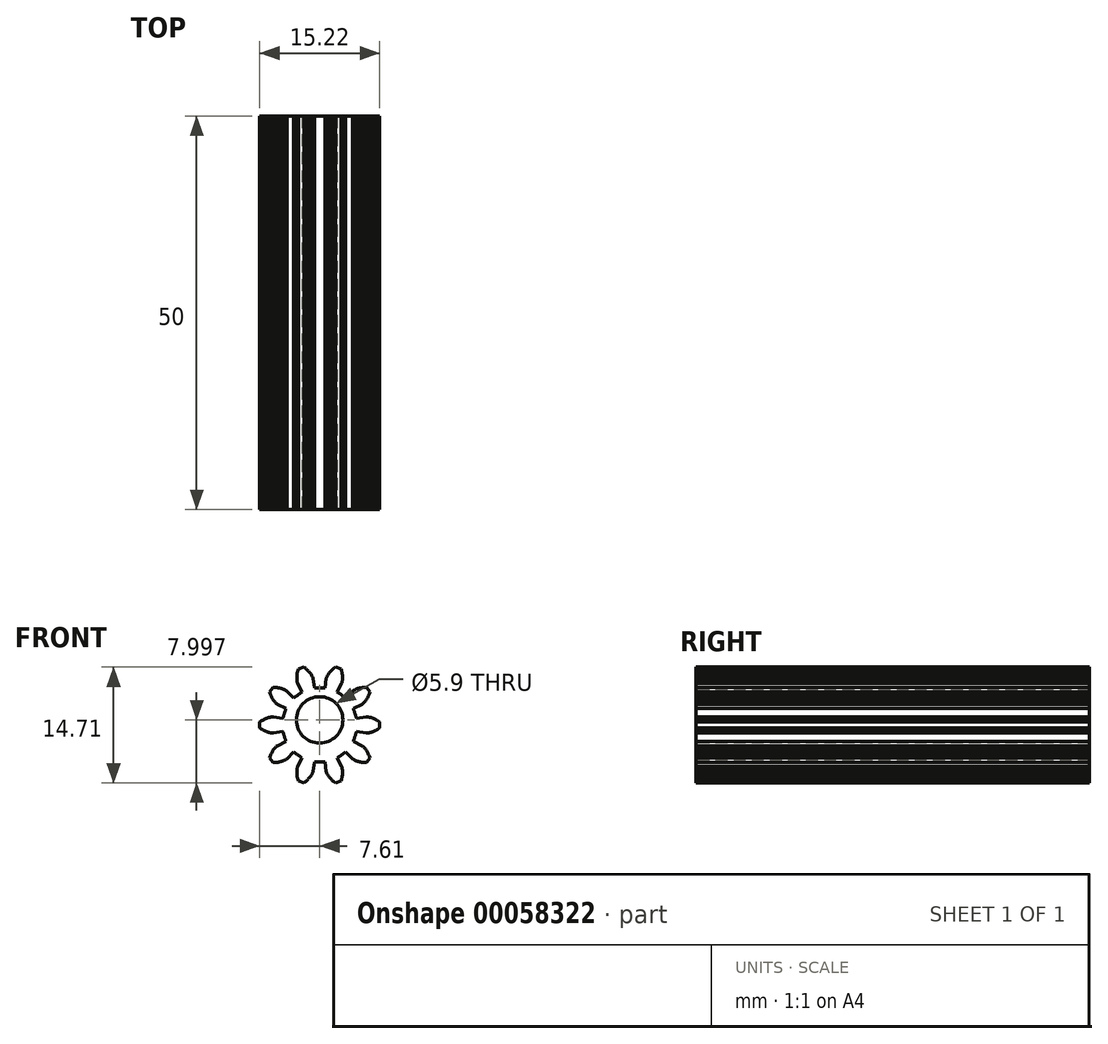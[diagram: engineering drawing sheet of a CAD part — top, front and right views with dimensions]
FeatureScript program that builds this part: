
annotation { "Feature Type Name" : "Feature", "Feature Type Description" : "" }
export const myFeature = defineFeature(function(context is Context, id is Id, definition is map)
    precondition{}
    {
        {
            var Q0;
            Q0=qCreatedBy(makeId("Front.planeOp"),FACE);
            var sketch = newSketch(context, id + "F0", { "sketchPlane" : qUnion([Q0])});
            skLineSegment(sketch, "E0", {"start": v(4.7, 0.36) * mm, "end": v(5.88, 0.15) * mm});
            skLineSegment(sketch, "E1", {"start": v(5.88, 0.15) * mm, "end": v(5.98, 0.15) * mm});
            skLineSegment(sketch, "E2", {"start": v(5.98, 0.15) * mm, "end": v(6.08, 0.15) * mm});
            skLineSegment(sketch, "E3", {"start": v(6.08, 0.15) * mm, "end": v(6.19, 0.17) * mm});
            skLineSegment(sketch, "E4", {"start": v(6.19, 0.17) * mm, "end": v(6.3, 0.19) * mm});
            skLineSegment(sketch, "E5", {"start": v(6.3, 0.19) * mm, "end": v(6.4, 0.2) * mm});
            skLineSegment(sketch, "E6", {"start": v(6.4, 0.2) * mm, "end": v(6.5, 0.24) * mm});
            skLineSegment(sketch, "E7", {"start": v(6.5, 0.24) * mm, "end": v(6.63, 0.28) * mm});
            skLineSegment(sketch, "E8", {"start": v(6.63, 0.28) * mm, "end": v(6.73, 0.32) * mm});
            skLineSegment(sketch, "E9", {"start": v(6.73, 0.32) * mm, "end": v(6.84, 0.36) * mm});
            skLineSegment(sketch, "E10", {"start": v(6.84, 0.36) * mm, "end": v(6.95, 0.4) * mm});
            skLineSegment(sketch, "E11", {"start": v(6.95, 0.4) * mm, "end": v(7.07, 0.47) * mm});
            skLineSegment(sketch, "E12", {"start": v(7.07, 0.47) * mm, "end": v(7.16, 0.52) * mm});
            skLineSegment(sketch, "E13", {"start": v(7.16, 0.52) * mm, "end": v(7.25, 0.57) * mm});
            skLineSegment(sketch, "E14", {"start": v(7.25, 0.57) * mm, "end": v(7.35, 0.63) * mm});
            skLineSegment(sketch, "E15", {"start": v(7.35, 0.63) * mm, "end": v(7.44, 0.69) * mm});
            skLineSegment(sketch, "E16", {"start": v(7.44, 0.69) * mm, "end": v(7.61, 0.8) * mm});
            skLineSegment(sketch, "E17", {"start": v(7.61, 0.8) * mm, "end": v(7.61, 1.55) * mm});
            skLineSegment(sketch, "E18", {"start": v(7.61, 1.55) * mm, "end": v(7.44, 1.66) * mm});
            skLineSegment(sketch, "E19", {"start": v(7.44, 1.66) * mm, "end": v(7.35, 1.72) * mm});
            skLineSegment(sketch, "E20", {"start": v(7.35, 1.72) * mm, "end": v(7.25, 1.78) * mm});
            skLineSegment(sketch, "E21", {"start": v(7.25, 1.78) * mm, "end": v(7.16, 1.83) * mm});
            skLineSegment(sketch, "E22", {"start": v(7.16, 1.83) * mm, "end": v(7.07, 1.88) * mm});
            skLineSegment(sketch, "E23", {"start": v(7.07, 1.88) * mm, "end": v(6.95, 1.94) * mm});
            skLineSegment(sketch, "E24", {"start": v(6.95, 1.94) * mm, "end": v(6.84, 1.99) * mm});
            skLineSegment(sketch, "E25", {"start": v(6.84, 1.99) * mm, "end": v(6.73, 2.03) * mm});
            skLineSegment(sketch, "E26", {"start": v(6.73, 2.03) * mm, "end": v(6.63, 2.07) * mm});
            skLineSegment(sketch, "E27", {"start": v(6.63, 2.07) * mm, "end": v(6.5, 2.1) * mm});
            skLineSegment(sketch, "E28", {"start": v(6.5, 2.1) * mm, "end": v(6.4, 2.14) * mm});
            skLineSegment(sketch, "E29", {"start": v(6.4, 2.14) * mm, "end": v(6.3, 2.16) * mm});
            skLineSegment(sketch, "E30", {"start": v(6.3, 2.16) * mm, "end": v(6.19, 2.18) * mm});
            skLineSegment(sketch, "E31", {"start": v(6.19, 2.18) * mm, "end": v(6.08, 2.2) * mm});
            skLineSegment(sketch, "E32", {"start": v(6.08, 2.2) * mm, "end": v(5.98, 2.2) * mm});
            skLineSegment(sketch, "E33", {"start": v(5.98, 2.2) * mm, "end": v(5.88, 2.2) * mm});
            skLineSegment(sketch, "E34", {"start": v(5.88, 2.2) * mm, "end": v(4.7, 1.99) * mm});
            skArc(sketch, "E35", {"start": v(4.7, 1.99) * mm, "mid": v(4.48, 2.63) * mm, "end": v(4.28, 3.27) * mm});
            skLineSegment(sketch, "E36", {"start": v(4.28, 3.27) * mm, "end": v(5.36, 3.8) * mm});
            skLineSegment(sketch, "E37", {"start": v(5.36, 3.8) * mm, "end": v(5.44, 3.86) * mm});
            skLineSegment(sketch, "E38", {"start": v(5.44, 3.86) * mm, "end": v(5.52, 3.92) * mm});
            skLineSegment(sketch, "E39", {"start": v(5.52, 3.92) * mm, "end": v(5.6, 4) * mm});
            skLineSegment(sketch, "E40", {"start": v(5.6, 4) * mm, "end": v(5.67, 4.08) * mm});
            skLineSegment(sketch, "E41", {"start": v(5.67, 4.08) * mm, "end": v(5.74, 4.15) * mm});
            skLineSegment(sketch, "E42", {"start": v(5.74, 4.15) * mm, "end": v(5.81, 4.24) * mm});
            skLineSegment(sketch, "E43", {"start": v(5.81, 4.24) * mm, "end": v(5.89, 4.34) * mm});
            skLineSegment(sketch, "E44", {"start": v(5.89, 4.34) * mm, "end": v(5.95, 4.44) * mm});
            skLineSegment(sketch, "E45", {"start": v(5.95, 4.44) * mm, "end": v(6.01, 4.53) * mm});
            skLineSegment(sketch, "E46", {"start": v(6.01, 4.53) * mm, "end": v(6.07, 4.64) * mm});
            skLineSegment(sketch, "E47", {"start": v(6.07, 4.64) * mm, "end": v(6.13, 4.76) * mm});
            skLineSegment(sketch, "E48", {"start": v(6.13, 4.76) * mm, "end": v(6.18, 4.85) * mm});
            skLineSegment(sketch, "E49", {"start": v(6.18, 4.85) * mm, "end": v(6.22, 4.95) * mm});
            skLineSegment(sketch, "E50", {"start": v(6.22, 4.95) * mm, "end": v(6.27, 5.05) * mm});
            skLineSegment(sketch, "E51", {"start": v(6.27, 5.05) * mm, "end": v(6.3, 5.16) * mm});
            skLineSegment(sketch, "E52", {"start": v(6.3, 5.16) * mm, "end": v(6.38, 5.35) * mm});
            skLineSegment(sketch, "E53", {"start": v(6.38, 5.35) * mm, "end": v(5.94, 5.95) * mm});
            skLineSegment(sketch, "E54", {"start": v(5.94, 5.95) * mm, "end": v(5.74, 5.94) * mm});
            skLineSegment(sketch, "E55", {"start": v(5.74, 5.94) * mm, "end": v(5.62, 5.94) * mm});
            skLineSegment(sketch, "E56", {"start": v(5.62, 5.94) * mm, "end": v(5.51, 5.93) * mm});
            skLineSegment(sketch, "E57", {"start": v(5.51, 5.93) * mm, "end": v(5.4, 5.92) * mm});
            skLineSegment(sketch, "E58", {"start": v(5.4, 5.92) * mm, "end": v(5.3, 5.9) * mm});
            skLineSegment(sketch, "E59", {"start": v(5.3, 5.9) * mm, "end": v(5.17, 5.88) * mm});
            skLineSegment(sketch, "E60", {"start": v(5.17, 5.88) * mm, "end": v(5.05, 5.85) * mm});
            skLineSegment(sketch, "E61", {"start": v(5.05, 5.85) * mm, "end": v(4.94, 5.83) * mm});
            skLineSegment(sketch, "E62", {"start": v(4.94, 5.83) * mm, "end": v(4.83, 5.8) * mm});
            skLineSegment(sketch, "E63", {"start": v(4.83, 5.8) * mm, "end": v(4.71, 5.76) * mm});
            skLineSegment(sketch, "E64", {"start": v(4.71, 5.76) * mm, "end": v(4.6, 5.72) * mm});
            skLineSegment(sketch, "E65", {"start": v(4.6, 5.72) * mm, "end": v(4.51, 5.68) * mm});
            skLineSegment(sketch, "E66", {"start": v(4.51, 5.68) * mm, "end": v(4.41, 5.63) * mm});
            skLineSegment(sketch, "E67", {"start": v(4.41, 5.63) * mm, "end": v(4.32, 5.58) * mm});
            skLineSegment(sketch, "E68", {"start": v(4.32, 5.58) * mm, "end": v(4.23, 5.52) * mm});
            skLineSegment(sketch, "E69", {"start": v(4.23, 5.52) * mm, "end": v(4.16, 5.46) * mm});
            skLineSegment(sketch, "E70", {"start": v(4.16, 5.46) * mm, "end": v(3.32, 4.6) * mm});
            skArc(sketch, "E71", {"start": v(3.32, 4.6) * mm, "mid": v(2.77, 4.99) * mm, "end": v(2.23, 5.39) * mm});
            skLineSegment(sketch, "E72", {"start": v(2.23, 5.39) * mm, "end": v(2.79, 6.45) * mm});
            skLineSegment(sketch, "E73", {"start": v(2.79, 6.45) * mm, "end": v(2.82, 6.54) * mm});
            skLineSegment(sketch, "E74", {"start": v(2.82, 6.54) * mm, "end": v(2.85, 6.64) * mm});
            skLineSegment(sketch, "E75", {"start": v(2.85, 6.64) * mm, "end": v(2.87, 6.75) * mm});
            skLineSegment(sketch, "E76", {"start": v(2.87, 6.75) * mm, "end": v(2.89, 6.86) * mm});
            skLineSegment(sketch, "E77", {"start": v(2.89, 6.86) * mm, "end": v(2.9, 6.96) * mm});
            skLineSegment(sketch, "E78", {"start": v(2.9, 6.96) * mm, "end": v(2.9, 7.07) * mm});
            skLineSegment(sketch, "E79", {"start": v(2.9, 7.07) * mm, "end": v(2.9, 7.2) * mm});
            skLineSegment(sketch, "E80", {"start": v(2.9, 7.2) * mm, "end": v(2.9, 7.3) * mm});
            skLineSegment(sketch, "E81", {"start": v(2.9, 7.3) * mm, "end": v(2.89, 7.43) * mm});
            skLineSegment(sketch, "E82", {"start": v(2.89, 7.43) * mm, "end": v(2.87, 7.55) * mm});
            skLineSegment(sketch, "E83", {"start": v(2.87, 7.55) * mm, "end": v(2.86, 7.68) * mm});
            skLineSegment(sketch, "E84", {"start": v(2.86, 7.68) * mm, "end": v(2.84, 7.78) * mm});
            skLineSegment(sketch, "E85", {"start": v(2.84, 7.78) * mm, "end": v(2.82, 7.88) * mm});
            skLineSegment(sketch, "E86", {"start": v(2.82, 7.88) * mm, "end": v(2.8, 8) * mm});
            skLineSegment(sketch, "E87", {"start": v(2.8, 8) * mm, "end": v(2.76, 8.1) * mm});
            skLineSegment(sketch, "E88", {"start": v(2.76, 8.1) * mm, "end": v(2.7, 8.3) * mm});
            skLineSegment(sketch, "E89", {"start": v(2.7, 8.3) * mm, "end": v(2, 8.53) * mm});
            skLineSegment(sketch, "E90", {"start": v(2, 8.53) * mm, "end": v(1.84, 8.4) * mm});
            skLineSegment(sketch, "E91", {"start": v(1.84, 8.4) * mm, "end": v(1.75, 8.33) * mm});
            skLineSegment(sketch, "E92", {"start": v(1.75, 8.33) * mm, "end": v(1.66, 8.26) * mm});
            skLineSegment(sketch, "E93", {"start": v(1.66, 8.26) * mm, "end": v(1.59, 8.19) * mm});
            skLineSegment(sketch, "E94", {"start": v(1.59, 8.19) * mm, "end": v(1.51, 8.11) * mm});
            skLineSegment(sketch, "E95", {"start": v(1.51, 8.11) * mm, "end": v(1.42, 8.02) * mm});
            skLineSegment(sketch, "E96", {"start": v(1.42, 8.02) * mm, "end": v(1.34, 7.93) * mm});
            skLineSegment(sketch, "E97", {"start": v(1.34, 7.93) * mm, "end": v(1.26, 7.84) * mm});
            skLineSegment(sketch, "E98", {"start": v(1.26, 7.84) * mm, "end": v(1.2, 7.75) * mm});
            skLineSegment(sketch, "E99", {"start": v(1.2, 7.75) * mm, "end": v(1.12, 7.65) * mm});
            skLineSegment(sketch, "E100", {"start": v(1.12, 7.65) * mm, "end": v(1.06, 7.56) * mm});
            skLineSegment(sketch, "E101", {"start": v(1.06, 7.56) * mm, "end": v(1, 7.47) * mm});
            skLineSegment(sketch, "E102", {"start": v(1, 7.47) * mm, "end": v(0.95, 7.37) * mm});
            skLineSegment(sketch, "E103", {"start": v(0.95, 7.37) * mm, "end": v(0.9, 7.28) * mm});
            skLineSegment(sketch, "E104", {"start": v(0.9, 7.28) * mm, "end": v(0.87, 7.18) * mm});
            skLineSegment(sketch, "E105", {"start": v(0.87, 7.18) * mm, "end": v(0.85, 7.08) * mm});
            skLineSegment(sketch, "E106", {"start": v(0.85, 7.08) * mm, "end": v(0.67, 5.89) * mm});
            skArc(sketch, "E107", {"start": v(0.67, 5.89) * mm, "mid": v(0, 5.89) * mm, "end": v(-0.67, 5.89) * mm});
            skLineSegment(sketch, "E108", {"start": v(-0.67, 5.89) * mm, "end": v(-0.85, 7.08) * mm});
            skLineSegment(sketch, "E109", {"start": v(-0.85, 7.08) * mm, "end": v(-0.87, 7.18) * mm});
            skLineSegment(sketch, "E110", {"start": v(-0.87, 7.18) * mm, "end": v(-0.9, 7.28) * mm});
            skLineSegment(sketch, "E111", {"start": v(-0.9, 7.28) * mm, "end": v(-0.95, 7.37) * mm});
            skLineSegment(sketch, "E112", {"start": v(-0.95, 7.37) * mm, "end": v(-1, 7.47) * mm});
            skLineSegment(sketch, "E113", {"start": v(-1, 7.47) * mm, "end": v(-1.06, 7.56) * mm});
            skLineSegment(sketch, "E114", {"start": v(-1.06, 7.56) * mm, "end": v(-1.12, 7.65) * mm});
            skLineSegment(sketch, "E115", {"start": v(-1.12, 7.65) * mm, "end": v(-1.2, 7.75) * mm});
            skLineSegment(sketch, "E116", {"start": v(-1.2, 7.75) * mm, "end": v(-1.26, 7.84) * mm});
            skLineSegment(sketch, "E117", {"start": v(-1.26, 7.84) * mm, "end": v(-1.34, 7.93) * mm});
            skLineSegment(sketch, "E118", {"start": v(-1.34, 7.93) * mm, "end": v(-1.42, 8.02) * mm});
            skLineSegment(sketch, "E119", {"start": v(-1.42, 8.02) * mm, "end": v(-1.51, 8.11) * mm});
            skLineSegment(sketch, "E120", {"start": v(-1.51, 8.11) * mm, "end": v(-1.59, 8.19) * mm});
            skLineSegment(sketch, "E121", {"start": v(-1.59, 8.19) * mm, "end": v(-1.66, 8.26) * mm});
            skLineSegment(sketch, "E122", {"start": v(-1.66, 8.26) * mm, "end": v(-1.75, 8.33) * mm});
            skLineSegment(sketch, "E123", {"start": v(-1.75, 8.33) * mm, "end": v(-1.84, 8.4) * mm});
            skLineSegment(sketch, "E124", {"start": v(-1.84, 8.4) * mm, "end": v(-2, 8.53) * mm});
            skLineSegment(sketch, "E125", {"start": v(-2, 8.53) * mm, "end": v(-2.7, 8.3) * mm});
            skLineSegment(sketch, "E126", {"start": v(-2.7, 8.3) * mm, "end": v(-2.76, 8.1) * mm});
            skLineSegment(sketch, "E127", {"start": v(-2.76, 8.1) * mm, "end": v(-2.8, 8) * mm});
            skLineSegment(sketch, "E128", {"start": v(-2.8, 8) * mm, "end": v(-2.82, 7.88) * mm});
            skLineSegment(sketch, "E129", {"start": v(-2.82, 7.88) * mm, "end": v(-2.84, 7.78) * mm});
            skLineSegment(sketch, "E130", {"start": v(-2.84, 7.78) * mm, "end": v(-2.86, 7.68) * mm});
            skLineSegment(sketch, "E131", {"start": v(-2.86, 7.68) * mm, "end": v(-2.87, 7.55) * mm});
            skLineSegment(sketch, "E132", {"start": v(-2.87, 7.55) * mm, "end": v(-2.89, 7.43) * mm});
            skLineSegment(sketch, "E133", {"start": v(-2.89, 7.43) * mm, "end": v(-2.9, 7.3) * mm});
            skLineSegment(sketch, "E134", {"start": v(-2.9, 7.3) * mm, "end": v(-2.9, 7.2) * mm});
            skLineSegment(sketch, "E135", {"start": v(-2.9, 7.2) * mm, "end": v(-2.9, 7.07) * mm});
            skLineSegment(sketch, "E136", {"start": v(-2.9, 7.07) * mm, "end": v(-2.9, 6.96) * mm});
            skLineSegment(sketch, "E137", {"start": v(-2.9, 6.96) * mm, "end": v(-2.89, 6.86) * mm});
            skLineSegment(sketch, "E138", {"start": v(-2.89, 6.86) * mm, "end": v(-2.87, 6.75) * mm});
            skLineSegment(sketch, "E139", {"start": v(-2.87, 6.75) * mm, "end": v(-2.85, 6.64) * mm});
            skLineSegment(sketch, "E140", {"start": v(-2.85, 6.64) * mm, "end": v(-2.82, 6.54) * mm});
            skLineSegment(sketch, "E141", {"start": v(-2.82, 6.54) * mm, "end": v(-2.79, 6.45) * mm});
            skLineSegment(sketch, "E142", {"start": v(-2.79, 6.45) * mm, "end": v(-2.23, 5.39) * mm});
            skArc(sketch, "E143", {"start": v(-2.23, 5.39) * mm, "mid": v(-2.77, 4.99) * mm, "end": v(-3.32, 4.6) * mm});
            skLineSegment(sketch, "E144", {"start": v(-3.32, 4.6) * mm, "end": v(-4.16, 5.46) * mm});
            skLineSegment(sketch, "E145", {"start": v(-4.16, 5.46) * mm, "end": v(-4.23, 5.52) * mm});
            skLineSegment(sketch, "E146", {"start": v(-4.23, 5.52) * mm, "end": v(-4.32, 5.58) * mm});
            skLineSegment(sketch, "E147", {"start": v(-4.32, 5.58) * mm, "end": v(-4.41, 5.63) * mm});
            skLineSegment(sketch, "E148", {"start": v(-4.41, 5.63) * mm, "end": v(-4.51, 5.68) * mm});
            skLineSegment(sketch, "E149", {"start": v(-4.51, 5.68) * mm, "end": v(-4.6, 5.72) * mm});
            skLineSegment(sketch, "E150", {"start": v(-4.6, 5.72) * mm, "end": v(-4.71, 5.76) * mm});
            skLineSegment(sketch, "E151", {"start": v(-4.71, 5.76) * mm, "end": v(-4.83, 5.8) * mm});
            skLineSegment(sketch, "E152", {"start": v(-4.83, 5.8) * mm, "end": v(-4.94, 5.83) * mm});
            skLineSegment(sketch, "E153", {"start": v(-4.94, 5.83) * mm, "end": v(-5.05, 5.85) * mm});
            skLineSegment(sketch, "E154", {"start": v(-5.05, 5.85) * mm, "end": v(-5.17, 5.88) * mm});
            skLineSegment(sketch, "E155", {"start": v(-5.17, 5.88) * mm, "end": v(-5.3, 5.9) * mm});
            skLineSegment(sketch, "E156", {"start": v(-5.3, 5.9) * mm, "end": v(-5.4, 5.92) * mm});
            skLineSegment(sketch, "E157", {"start": v(-5.4, 5.92) * mm, "end": v(-5.51, 5.93) * mm});
            skLineSegment(sketch, "E158", {"start": v(-5.51, 5.93) * mm, "end": v(-5.62, 5.94) * mm});
            skLineSegment(sketch, "E159", {"start": v(-5.62, 5.94) * mm, "end": v(-5.74, 5.94) * mm});
            skLineSegment(sketch, "E160", {"start": v(-5.74, 5.94) * mm, "end": v(-5.94, 5.95) * mm});
            skLineSegment(sketch, "E161", {"start": v(-5.94, 5.95) * mm, "end": v(-6.38, 5.35) * mm});
            skLineSegment(sketch, "E162", {"start": v(-6.38, 5.35) * mm, "end": v(-6.3, 5.16) * mm});
            skLineSegment(sketch, "E163", {"start": v(-6.3, 5.16) * mm, "end": v(-6.27, 5.05) * mm});
            skLineSegment(sketch, "E164", {"start": v(-6.27, 5.05) * mm, "end": v(-6.22, 4.95) * mm});
            skLineSegment(sketch, "E165", {"start": v(-6.22, 4.95) * mm, "end": v(-6.18, 4.85) * mm});
            skLineSegment(sketch, "E166", {"start": v(-6.18, 4.85) * mm, "end": v(-6.13, 4.76) * mm});
            skLineSegment(sketch, "E167", {"start": v(-6.13, 4.76) * mm, "end": v(-6.07, 4.64) * mm});
            skLineSegment(sketch, "E168", {"start": v(-6.07, 4.64) * mm, "end": v(-6.01, 4.53) * mm});
            skLineSegment(sketch, "E169", {"start": v(-6.01, 4.53) * mm, "end": v(-5.95, 4.44) * mm});
            skLineSegment(sketch, "E170", {"start": v(-5.95, 4.44) * mm, "end": v(-5.89, 4.34) * mm});
            skLineSegment(sketch, "E171", {"start": v(-5.89, 4.34) * mm, "end": v(-5.81, 4.24) * mm});
            skLineSegment(sketch, "E172", {"start": v(-5.81, 4.24) * mm, "end": v(-5.74, 4.15) * mm});
            skLineSegment(sketch, "E173", {"start": v(-5.74, 4.15) * mm, "end": v(-5.67, 4.08) * mm});
            skLineSegment(sketch, "E174", {"start": v(-5.67, 4.08) * mm, "end": v(-5.6, 4) * mm});
            skLineSegment(sketch, "E175", {"start": v(-5.6, 4) * mm, "end": v(-5.52, 3.92) * mm});
            skLineSegment(sketch, "E176", {"start": v(-5.52, 3.92) * mm, "end": v(-5.44, 3.86) * mm});
            skLineSegment(sketch, "E177", {"start": v(-5.44, 3.86) * mm, "end": v(-5.36, 3.8) * mm});
            skLineSegment(sketch, "E178", {"start": v(-5.36, 3.8) * mm, "end": v(-4.28, 3.27) * mm});
            skArc(sketch, "E179", {"start": v(-4.28, 3.27) * mm, "mid": v(-4.48, 2.63) * mm, "end": v(-4.7, 1.99) * mm});
            skLineSegment(sketch, "E180", {"start": v(-4.7, 1.99) * mm, "end": v(-5.88, 2.2) * mm});
            skLineSegment(sketch, "E181", {"start": v(-5.88, 2.2) * mm, "end": v(-5.98, 2.2) * mm});
            skLineSegment(sketch, "E182", {"start": v(-5.98, 2.2) * mm, "end": v(-6.08, 2.2) * mm});
            skLineSegment(sketch, "E183", {"start": v(-6.08, 2.2) * mm, "end": v(-6.19, 2.18) * mm});
            skLineSegment(sketch, "E184", {"start": v(-6.19, 2.18) * mm, "end": v(-6.3, 2.16) * mm});
            skLineSegment(sketch, "E185", {"start": v(-6.3, 2.16) * mm, "end": v(-6.4, 2.14) * mm});
            skLineSegment(sketch, "E186", {"start": v(-6.4, 2.14) * mm, "end": v(-6.5, 2.1) * mm});
            skLineSegment(sketch, "E187", {"start": v(-6.5, 2.1) * mm, "end": v(-6.63, 2.07) * mm});
            skLineSegment(sketch, "E188", {"start": v(-6.63, 2.07) * mm, "end": v(-6.73, 2.03) * mm});
            skLineSegment(sketch, "E189", {"start": v(-6.73, 2.03) * mm, "end": v(-6.84, 1.99) * mm});
            skLineSegment(sketch, "E190", {"start": v(-6.84, 1.99) * mm, "end": v(-6.95, 1.94) * mm});
            skLineSegment(sketch, "E191", {"start": v(-6.95, 1.94) * mm, "end": v(-7.07, 1.88) * mm});
            skLineSegment(sketch, "E192", {"start": v(-7.07, 1.88) * mm, "end": v(-7.16, 1.83) * mm});
            skLineSegment(sketch, "E193", {"start": v(-7.16, 1.83) * mm, "end": v(-7.25, 1.78) * mm});
            skLineSegment(sketch, "E194", {"start": v(-7.25, 1.78) * mm, "end": v(-7.35, 1.72) * mm});
            skLineSegment(sketch, "E195", {"start": v(-7.35, 1.72) * mm, "end": v(-7.44, 1.66) * mm});
            skLineSegment(sketch, "E196", {"start": v(-7.44, 1.66) * mm, "end": v(-7.61, 1.55) * mm});
            skLineSegment(sketch, "E197", {"start": v(-7.61, 1.55) * mm, "end": v(-7.61, 0.8) * mm});
            skLineSegment(sketch, "E198", {"start": v(-7.61, 0.8) * mm, "end": v(-7.44, 0.69) * mm});
            skLineSegment(sketch, "E199", {"start": v(-7.44, 0.69) * mm, "end": v(-7.35, 0.63) * mm});
            skLineSegment(sketch, "E200", {"start": v(-7.35, 0.63) * mm, "end": v(-7.25, 0.57) * mm});
            skLineSegment(sketch, "E201", {"start": v(-7.25, 0.57) * mm, "end": v(-7.16, 0.52) * mm});
            skLineSegment(sketch, "E202", {"start": v(-7.16, 0.52) * mm, "end": v(-7.07, 0.47) * mm});
            skLineSegment(sketch, "E203", {"start": v(-7.07, 0.47) * mm, "end": v(-6.95, 0.4) * mm});
            skLineSegment(sketch, "E204", {"start": v(-6.95, 0.4) * mm, "end": v(-6.84, 0.36) * mm});
            skLineSegment(sketch, "E205", {"start": v(-6.84, 0.36) * mm, "end": v(-6.73, 0.32) * mm});
            skLineSegment(sketch, "E206", {"start": v(-6.73, 0.32) * mm, "end": v(-6.63, 0.28) * mm});
            skLineSegment(sketch, "E207", {"start": v(-6.63, 0.28) * mm, "end": v(-6.5, 0.24) * mm});
            skLineSegment(sketch, "E208", {"start": v(-6.5, 0.24) * mm, "end": v(-6.4, 0.2) * mm});
            skLineSegment(sketch, "E209", {"start": v(-6.4, 0.2) * mm, "end": v(-6.3, 0.19) * mm});
            skLineSegment(sketch, "E210", {"start": v(-6.3, 0.19) * mm, "end": v(-6.19, 0.17) * mm});
            skLineSegment(sketch, "E211", {"start": v(-6.19, 0.17) * mm, "end": v(-6.08, 0.15) * mm});
            skLineSegment(sketch, "E212", {"start": v(-6.08, 0.15) * mm, "end": v(-5.98, 0.15) * mm});
            skLineSegment(sketch, "E213", {"start": v(-5.98, 0.15) * mm, "end": v(-5.88, 0.15) * mm});
            skLineSegment(sketch, "E214", {"start": v(-5.88, 0.15) * mm, "end": v(-4.7, 0.36) * mm});
            skArc(sketch, "E215", {"start": v(-4.7, 0.36) * mm, "mid": v(-4.48, -0.28) * mm, "end": v(-4.28, -0.92) * mm});
            skLineSegment(sketch, "E216", {"start": v(-4.28, -0.92) * mm, "end": v(-5.36, -1.45) * mm});
            skLineSegment(sketch, "E217", {"start": v(-5.36, -1.45) * mm, "end": v(-5.44, -1.5) * mm});
            skLineSegment(sketch, "E218", {"start": v(-5.44, -1.5) * mm, "end": v(-5.52, -1.57) * mm});
            skLineSegment(sketch, "E219", {"start": v(-5.52, -1.57) * mm, "end": v(-5.6, -1.65) * mm});
            skLineSegment(sketch, "E220", {"start": v(-5.6, -1.65) * mm, "end": v(-5.67, -1.73) * mm});
            skLineSegment(sketch, "E221", {"start": v(-5.67, -1.73) * mm, "end": v(-5.74, -1.8) * mm});
            skLineSegment(sketch, "E222", {"start": v(-5.74, -1.8) * mm, "end": v(-5.81, -1.9) * mm});
            skLineSegment(sketch, "E223", {"start": v(-5.81, -1.9) * mm, "end": v(-5.89, -2) * mm});
            skLineSegment(sketch, "E224", {"start": v(-5.89, -2) * mm, "end": v(-5.95, -2.09) * mm});
            skLineSegment(sketch, "E225", {"start": v(-5.95, -2.09) * mm, "end": v(-6.01, -2.18) * mm});
            skLineSegment(sketch, "E226", {"start": v(-6.01, -2.18) * mm, "end": v(-6.07, -2.3) * mm});
            skLineSegment(sketch, "E227", {"start": v(-6.07, -2.3) * mm, "end": v(-6.13, -2.4) * mm});
            skLineSegment(sketch, "E228", {"start": v(-6.13, -2.4) * mm, "end": v(-6.18, -2.5) * mm});
            skLineSegment(sketch, "E229", {"start": v(-6.18, -2.5) * mm, "end": v(-6.22, -2.6) * mm});
            skLineSegment(sketch, "E230", {"start": v(-6.22, -2.6) * mm, "end": v(-6.27, -2.7) * mm});
            skLineSegment(sketch, "E231", {"start": v(-6.27, -2.7) * mm, "end": v(-6.3, -2.8) * mm});
            skLineSegment(sketch, "E232", {"start": v(-6.3, -2.8) * mm, "end": v(-6.38, -3) * mm});
            skLineSegment(sketch, "E233", {"start": v(-6.38, -3) * mm, "end": v(-5.94, -3.6) * mm});
            skLineSegment(sketch, "E234", {"start": v(-5.94, -3.6) * mm, "end": v(-5.74, -3.6) * mm});
            skLineSegment(sketch, "E235", {"start": v(-5.74, -3.6) * mm, "end": v(-5.62, -3.59) * mm});
            skLineSegment(sketch, "E236", {"start": v(-5.62, -3.59) * mm, "end": v(-5.51, -3.58) * mm});
            skLineSegment(sketch, "E237", {"start": v(-5.51, -3.58) * mm, "end": v(-5.4, -3.57) * mm});
            skLineSegment(sketch, "E238", {"start": v(-5.4, -3.57) * mm, "end": v(-5.3, -3.55) * mm});
            skLineSegment(sketch, "E239", {"start": v(-5.3, -3.55) * mm, "end": v(-5.17, -3.53) * mm});
            skLineSegment(sketch, "E240", {"start": v(-5.17, -3.53) * mm, "end": v(-5.05, -3.5) * mm});
            skLineSegment(sketch, "E241", {"start": v(-5.05, -3.5) * mm, "end": v(-4.94, -3.48) * mm});
            skLineSegment(sketch, "E242", {"start": v(-4.94, -3.48) * mm, "end": v(-4.83, -3.45) * mm});
            skLineSegment(sketch, "E243", {"start": v(-4.83, -3.45) * mm, "end": v(-4.71, -3.4) * mm});
            skLineSegment(sketch, "E244", {"start": v(-4.71, -3.4) * mm, "end": v(-4.6, -3.37) * mm});
            skLineSegment(sketch, "E245", {"start": v(-4.6, -3.37) * mm, "end": v(-4.51, -3.33) * mm});
            skLineSegment(sketch, "E246", {"start": v(-4.51, -3.33) * mm, "end": v(-4.41, -3.28) * mm});
            skLineSegment(sketch, "E247", {"start": v(-4.41, -3.28) * mm, "end": v(-4.32, -3.23) * mm});
            skLineSegment(sketch, "E248", {"start": v(-4.32, -3.23) * mm, "end": v(-4.23, -3.17) * mm});
            skLineSegment(sketch, "E249", {"start": v(-4.23, -3.17) * mm, "end": v(-4.16, -3.1) * mm});
            skLineSegment(sketch, "E250", {"start": v(-4.16, -3.1) * mm, "end": v(-3.32, -2.24) * mm});
            skArc(sketch, "E251", {"start": v(-3.32, -2.24) * mm, "mid": v(-2.77, -2.64) * mm, "end": v(-2.23, -3.04) * mm});
            skLineSegment(sketch, "E252", {"start": v(-2.23, -3.04) * mm, "end": v(-2.79, -4.1) * mm});
            skLineSegment(sketch, "E253", {"start": v(-2.79, -4.1) * mm, "end": v(-2.82, -4.2) * mm});
            skLineSegment(sketch, "E254", {"start": v(-2.82, -4.2) * mm, "end": v(-2.85, -4.3) * mm});
            skLineSegment(sketch, "E255", {"start": v(-2.85, -4.3) * mm, "end": v(-2.87, -4.4) * mm});
            skLineSegment(sketch, "E256", {"start": v(-2.87, -4.4) * mm, "end": v(-2.89, -4.5) * mm});
            skLineSegment(sketch, "E257", {"start": v(-2.89, -4.5) * mm, "end": v(-2.9, -4.61) * mm});
            skLineSegment(sketch, "E258", {"start": v(-2.9, -4.61) * mm, "end": v(-2.9, -4.73) * mm});
            skLineSegment(sketch, "E259", {"start": v(-2.9, -4.73) * mm, "end": v(-2.9, -4.85) * mm});
            skLineSegment(sketch, "E260", {"start": v(-2.9, -4.85) * mm, "end": v(-2.9, -4.96) * mm});
            skLineSegment(sketch, "E261", {"start": v(-2.9, -4.96) * mm, "end": v(-2.89, -5.08) * mm});
            skLineSegment(sketch, "E262", {"start": v(-2.89, -5.08) * mm, "end": v(-2.87, -5.2) * mm});
            skLineSegment(sketch, "E263", {"start": v(-2.87, -5.2) * mm, "end": v(-2.86, -5.33) * mm});
            skLineSegment(sketch, "E264", {"start": v(-2.86, -5.33) * mm, "end": v(-2.84, -5.43) * mm});
            skLineSegment(sketch, "E265", {"start": v(-2.84, -5.43) * mm, "end": v(-2.82, -5.54) * mm});
            skLineSegment(sketch, "E266", {"start": v(-2.82, -5.54) * mm, "end": v(-2.8, -5.64) * mm});
            skLineSegment(sketch, "E267", {"start": v(-2.8, -5.64) * mm, "end": v(-2.76, -5.76) * mm});
            skLineSegment(sketch, "E268", {"start": v(-2.76, -5.76) * mm, "end": v(-2.7, -5.95) * mm});
            skLineSegment(sketch, "E269", {"start": v(-2.7, -5.95) * mm, "end": v(-2, -6.18) * mm});
            skLineSegment(sketch, "E270", {"start": v(-2, -6.18) * mm, "end": v(-1.84, -6.06) * mm});
            skLineSegment(sketch, "E271", {"start": v(-1.84, -6.06) * mm, "end": v(-1.75, -5.98) * mm});
            skLineSegment(sketch, "E272", {"start": v(-1.75, -5.98) * mm, "end": v(-1.66, -5.9) * mm});
            skLineSegment(sketch, "E273", {"start": v(-1.66, -5.9) * mm, "end": v(-1.59, -5.84) * mm});
            skLineSegment(sketch, "E274", {"start": v(-1.59, -5.84) * mm, "end": v(-1.51, -5.77) * mm});
            skLineSegment(sketch, "E275", {"start": v(-1.51, -5.77) * mm, "end": v(-1.42, -5.67) * mm});
            skLineSegment(sketch, "E276", {"start": v(-1.42, -5.67) * mm, "end": v(-1.34, -5.58) * mm});
            skLineSegment(sketch, "E277", {"start": v(-1.34, -5.58) * mm, "end": v(-1.26, -5.5) * mm});
            skLineSegment(sketch, "E278", {"start": v(-1.26, -5.5) * mm, "end": v(-1.2, -5.4) * mm});
            skLineSegment(sketch, "E279", {"start": v(-1.2, -5.4) * mm, "end": v(-1.12, -5.3) * mm});
            skLineSegment(sketch, "E280", {"start": v(-1.12, -5.3) * mm, "end": v(-1.06, -5.2) * mm});
            skLineSegment(sketch, "E281", {"start": v(-1.06, -5.2) * mm, "end": v(-1, -5.12) * mm});
            skLineSegment(sketch, "E282", {"start": v(-1, -5.12) * mm, "end": v(-0.95, -5.02) * mm});
            skLineSegment(sketch, "E283", {"start": v(-0.95, -5.02) * mm, "end": v(-0.9, -4.93) * mm});
            skLineSegment(sketch, "E284", {"start": v(-0.9, -4.93) * mm, "end": v(-0.87, -4.83) * mm});
            skLineSegment(sketch, "E285", {"start": v(-0.87, -4.83) * mm, "end": v(-0.85, -4.73) * mm});
            skLineSegment(sketch, "E286", {"start": v(-0.85, -4.73) * mm, "end": v(-0.67, -3.54) * mm});
            skArc(sketch, "E287", {"start": v(-0.67, -3.54) * mm, "mid": v(0, -3.54) * mm, "end": v(0.67, -3.54) * mm});
            skLineSegment(sketch, "E288", {"start": v(0.67, -3.54) * mm, "end": v(0.85, -4.73) * mm});
            skLineSegment(sketch, "E289", {"start": v(0.85, -4.73) * mm, "end": v(0.87, -4.83) * mm});
            skLineSegment(sketch, "E290", {"start": v(0.87, -4.83) * mm, "end": v(0.9, -4.93) * mm});
            skLineSegment(sketch, "E291", {"start": v(0.9, -4.93) * mm, "end": v(0.95, -5.02) * mm});
            skLineSegment(sketch, "E292", {"start": v(0.95, -5.02) * mm, "end": v(1, -5.12) * mm});
            skLineSegment(sketch, "E293", {"start": v(1, -5.12) * mm, "end": v(1.06, -5.2) * mm});
            skLineSegment(sketch, "E294", {"start": v(1.06, -5.2) * mm, "end": v(1.12, -5.3) * mm});
            skLineSegment(sketch, "E295", {"start": v(1.12, -5.3) * mm, "end": v(1.2, -5.4) * mm});
            skLineSegment(sketch, "E296", {"start": v(1.2, -5.4) * mm, "end": v(1.26, -5.5) * mm});
            skLineSegment(sketch, "E297", {"start": v(1.26, -5.5) * mm, "end": v(1.34, -5.58) * mm});
            skLineSegment(sketch, "E298", {"start": v(1.34, -5.58) * mm, "end": v(1.42, -5.67) * mm});
            skLineSegment(sketch, "E299", {"start": v(1.42, -5.67) * mm, "end": v(1.51, -5.77) * mm});
            skLineSegment(sketch, "E300", {"start": v(1.51, -5.77) * mm, "end": v(1.59, -5.84) * mm});
            skLineSegment(sketch, "E301", {"start": v(1.59, -5.84) * mm, "end": v(1.66, -5.9) * mm});
            skLineSegment(sketch, "E302", {"start": v(1.66, -5.9) * mm, "end": v(1.75, -5.98) * mm});
            skLineSegment(sketch, "E303", {"start": v(1.75, -5.98) * mm, "end": v(1.84, -6.06) * mm});
            skLineSegment(sketch, "E304", {"start": v(1.84, -6.06) * mm, "end": v(2, -6.18) * mm});
            skLineSegment(sketch, "E305", {"start": v(2, -6.18) * mm, "end": v(2.7, -5.95) * mm});
            skLineSegment(sketch, "E306", {"start": v(2.7, -5.95) * mm, "end": v(2.76, -5.76) * mm});
            skLineSegment(sketch, "E307", {"start": v(2.76, -5.76) * mm, "end": v(2.8, -5.64) * mm});
            skLineSegment(sketch, "E308", {"start": v(2.8, -5.64) * mm, "end": v(2.82, -5.54) * mm});
            skLineSegment(sketch, "E309", {"start": v(2.82, -5.54) * mm, "end": v(2.84, -5.43) * mm});
            skLineSegment(sketch, "E310", {"start": v(2.84, -5.43) * mm, "end": v(2.86, -5.33) * mm});
            skLineSegment(sketch, "E311", {"start": v(2.86, -5.33) * mm, "end": v(2.87, -5.2) * mm});
            skLineSegment(sketch, "E312", {"start": v(2.87, -5.2) * mm, "end": v(2.89, -5.08) * mm});
            skLineSegment(sketch, "E313", {"start": v(2.89, -5.08) * mm, "end": v(2.9, -4.96) * mm});
            skLineSegment(sketch, "E314", {"start": v(2.9, -4.96) * mm, "end": v(2.9, -4.85) * mm});
            skLineSegment(sketch, "E315", {"start": v(2.9, -4.85) * mm, "end": v(2.9, -4.73) * mm});
            skLineSegment(sketch, "E316", {"start": v(2.9, -4.73) * mm, "end": v(2.9, -4.61) * mm});
            skLineSegment(sketch, "E317", {"start": v(2.9, -4.61) * mm, "end": v(2.89, -4.5) * mm});
            skLineSegment(sketch, "E318", {"start": v(2.89, -4.5) * mm, "end": v(2.87, -4.4) * mm});
            skLineSegment(sketch, "E319", {"start": v(2.87, -4.4) * mm, "end": v(2.85, -4.3) * mm});
            skLineSegment(sketch, "E320", {"start": v(2.85, -4.3) * mm, "end": v(2.82, -4.2) * mm});
            skLineSegment(sketch, "E321", {"start": v(2.82, -4.2) * mm, "end": v(2.79, -4.1) * mm});
            skLineSegment(sketch, "E322", {"start": v(2.79, -4.1) * mm, "end": v(2.23, -3.04) * mm});
            skArc(sketch, "E323", {"start": v(2.23, -3.04) * mm, "mid": v(2.77, -2.64) * mm, "end": v(3.32, -2.24) * mm});
            skLineSegment(sketch, "E324", {"start": v(3.32, -2.24) * mm, "end": v(4.16, -3.1) * mm});
            skLineSegment(sketch, "E325", {"start": v(4.16, -3.1) * mm, "end": v(4.23, -3.17) * mm});
            skLineSegment(sketch, "E326", {"start": v(4.23, -3.17) * mm, "end": v(4.32, -3.23) * mm});
            skLineSegment(sketch, "E327", {"start": v(4.32, -3.23) * mm, "end": v(4.41, -3.28) * mm});
            skLineSegment(sketch, "E328", {"start": v(4.41, -3.28) * mm, "end": v(4.51, -3.33) * mm});
            skLineSegment(sketch, "E329", {"start": v(4.51, -3.33) * mm, "end": v(4.6, -3.37) * mm});
            skLineSegment(sketch, "E330", {"start": v(4.6, -3.37) * mm, "end": v(4.71, -3.4) * mm});
            skLineSegment(sketch, "E331", {"start": v(4.71, -3.4) * mm, "end": v(4.83, -3.45) * mm});
            skLineSegment(sketch, "E332", {"start": v(4.83, -3.45) * mm, "end": v(4.94, -3.48) * mm});
            skLineSegment(sketch, "E333", {"start": v(4.94, -3.48) * mm, "end": v(5.05, -3.5) * mm});
            skLineSegment(sketch, "E334", {"start": v(5.05, -3.5) * mm, "end": v(5.17, -3.53) * mm});
            skLineSegment(sketch, "E335", {"start": v(5.17, -3.53) * mm, "end": v(5.3, -3.55) * mm});
            skLineSegment(sketch, "E336", {"start": v(5.3, -3.55) * mm, "end": v(5.4, -3.57) * mm});
            skLineSegment(sketch, "E337", {"start": v(5.4, -3.57) * mm, "end": v(5.51, -3.58) * mm});
            skLineSegment(sketch, "E338", {"start": v(5.51, -3.58) * mm, "end": v(5.62, -3.59) * mm});
            skLineSegment(sketch, "E339", {"start": v(5.62, -3.59) * mm, "end": v(5.74, -3.6) * mm});
            skLineSegment(sketch, "E340", {"start": v(5.74, -3.6) * mm, "end": v(5.94, -3.6) * mm});
            skLineSegment(sketch, "E341", {"start": v(5.94, -3.6) * mm, "end": v(6.38, -3) * mm});
            skLineSegment(sketch, "E342", {"start": v(6.38, -3) * mm, "end": v(6.3, -2.8) * mm});
            skLineSegment(sketch, "E343", {"start": v(6.3, -2.8) * mm, "end": v(6.27, -2.7) * mm});
            skLineSegment(sketch, "E344", {"start": v(6.27, -2.7) * mm, "end": v(6.22, -2.6) * mm});
            skLineSegment(sketch, "E345", {"start": v(6.22, -2.6) * mm, "end": v(6.18, -2.5) * mm});
            skLineSegment(sketch, "E346", {"start": v(6.18, -2.5) * mm, "end": v(6.13, -2.4) * mm});
            skLineSegment(sketch, "E347", {"start": v(6.13, -2.4) * mm, "end": v(6.07, -2.3) * mm});
            skLineSegment(sketch, "E348", {"start": v(6.07, -2.3) * mm, "end": v(6.01, -2.18) * mm});
            skLineSegment(sketch, "E349", {"start": v(6.01, -2.18) * mm, "end": v(5.95, -2.09) * mm});
            skLineSegment(sketch, "E350", {"start": v(5.95, -2.09) * mm, "end": v(5.89, -2) * mm});
            skLineSegment(sketch, "E351", {"start": v(5.89, -2) * mm, "end": v(5.81, -1.9) * mm});
            skLineSegment(sketch, "E352", {"start": v(5.81, -1.9) * mm, "end": v(5.74, -1.8) * mm});
            skLineSegment(sketch, "E353", {"start": v(5.74, -1.8) * mm, "end": v(5.67, -1.73) * mm});
            skLineSegment(sketch, "E354", {"start": v(5.67, -1.73) * mm, "end": v(5.6, -1.65) * mm});
            skLineSegment(sketch, "E355", {"start": v(5.6, -1.65) * mm, "end": v(5.52, -1.57) * mm});
            skLineSegment(sketch, "E356", {"start": v(5.52, -1.57) * mm, "end": v(5.44, -1.5) * mm});
            skLineSegment(sketch, "E357", {"start": v(5.44, -1.5) * mm, "end": v(5.36, -1.45) * mm});
            skLineSegment(sketch, "E358", {"start": v(5.36, -1.45) * mm, "end": v(4.28, -0.92) * mm});
            skArc(sketch, "E359", {"start": v(4.28, -0.92) * mm, "mid": v(4.48, -0.28) * mm, "end": v(4.7, 0.36) * mm});
            skSolve(sketch);
        }
        {
            var Q0;
            Q0=qCreatedBy(makeId("Front.planeOp"),FACE);
            cPlane(context, id + "F1", {"entities" : qUnion([Q0]), "cplaneType" : CPlaneType.OFFSET, "offset" : 50 * mm, "width" : 150 * mm, "height" : 150 * mm});
        }
        {
            var Q0;
            Q0=qCreatedBy(id+"F1.planeOp",FACE);
            var sketch = newSketch(context, id + "F2", { "sketchPlane" : qUnion([Q0])});
            skLineSegment(sketch, "E360", {"start": v(4.7, 0.36) * mm, "end": v(5.88, 0.15) * mm});
            skLineSegment(sketch, "E361", {"start": v(5.88, 0.15) * mm, "end": v(5.98, 0.15) * mm});
            skLineSegment(sketch, "E362", {"start": v(5.98, 0.15) * mm, "end": v(6.08, 0.15) * mm});
            skLineSegment(sketch, "E363", {"start": v(6.08, 0.15) * mm, "end": v(6.19, 0.17) * mm});
            skLineSegment(sketch, "E364", {"start": v(6.19, 0.17) * mm, "end": v(6.3, 0.19) * mm});
            skLineSegment(sketch, "E365", {"start": v(6.3, 0.19) * mm, "end": v(6.4, 0.2) * mm});
            skLineSegment(sketch, "E366", {"start": v(6.4, 0.2) * mm, "end": v(6.5, 0.24) * mm});
            skLineSegment(sketch, "E367", {"start": v(6.5, 0.24) * mm, "end": v(6.63, 0.28) * mm});
            skLineSegment(sketch, "E368", {"start": v(6.63, 0.28) * mm, "end": v(6.73, 0.32) * mm});
            skLineSegment(sketch, "E369", {"start": v(6.73, 0.32) * mm, "end": v(6.84, 0.36) * mm});
            skLineSegment(sketch, "E370", {"start": v(6.84, 0.36) * mm, "end": v(6.95, 0.4) * mm});
            skLineSegment(sketch, "E371", {"start": v(6.95, 0.4) * mm, "end": v(7.07, 0.47) * mm});
            skLineSegment(sketch, "E372", {"start": v(7.07, 0.47) * mm, "end": v(7.16, 0.52) * mm});
            skLineSegment(sketch, "E373", {"start": v(7.16, 0.52) * mm, "end": v(7.25, 0.57) * mm});
            skLineSegment(sketch, "E374", {"start": v(7.25, 0.57) * mm, "end": v(7.35, 0.63) * mm});
            skLineSegment(sketch, "E375", {"start": v(7.35, 0.63) * mm, "end": v(7.44, 0.69) * mm});
            skLineSegment(sketch, "E376", {"start": v(7.44, 0.69) * mm, "end": v(7.61, 0.8) * mm});
            skLineSegment(sketch, "E377", {"start": v(7.61, 0.8) * mm, "end": v(7.61, 1.55) * mm});
            skLineSegment(sketch, "E378", {"start": v(7.61, 1.55) * mm, "end": v(7.44, 1.66) * mm});
            skLineSegment(sketch, "E379", {"start": v(7.44, 1.66) * mm, "end": v(7.35, 1.72) * mm});
            skLineSegment(sketch, "E380", {"start": v(7.35, 1.72) * mm, "end": v(7.25, 1.78) * mm});
            skLineSegment(sketch, "E381", {"start": v(7.25, 1.78) * mm, "end": v(7.16, 1.83) * mm});
            skLineSegment(sketch, "E382", {"start": v(7.16, 1.83) * mm, "end": v(7.07, 1.88) * mm});
            skLineSegment(sketch, "E383", {"start": v(7.07, 1.88) * mm, "end": v(6.95, 1.94) * mm});
            skLineSegment(sketch, "E384", {"start": v(6.95, 1.94) * mm, "end": v(6.84, 1.99) * mm});
            skLineSegment(sketch, "E385", {"start": v(6.84, 1.99) * mm, "end": v(6.73, 2.03) * mm});
            skLineSegment(sketch, "E386", {"start": v(6.73, 2.03) * mm, "end": v(6.63, 2.07) * mm});
            skLineSegment(sketch, "E387", {"start": v(6.63, 2.07) * mm, "end": v(6.5, 2.1) * mm});
            skLineSegment(sketch, "E388", {"start": v(6.5, 2.1) * mm, "end": v(6.4, 2.14) * mm});
            skLineSegment(sketch, "E389", {"start": v(6.4, 2.14) * mm, "end": v(6.3, 2.16) * mm});
            skLineSegment(sketch, "E390", {"start": v(6.3, 2.16) * mm, "end": v(6.19, 2.18) * mm});
            skLineSegment(sketch, "E391", {"start": v(6.19, 2.18) * mm, "end": v(6.08, 2.2) * mm});
            skLineSegment(sketch, "E392", {"start": v(6.08, 2.2) * mm, "end": v(5.98, 2.2) * mm});
            skLineSegment(sketch, "E393", {"start": v(5.98, 2.2) * mm, "end": v(5.88, 2.2) * mm});
            skLineSegment(sketch, "E394", {"start": v(5.88, 2.2) * mm, "end": v(4.7, 1.99) * mm});
            skArc(sketch, "E395", {"start": v(4.7, 1.99) * mm, "mid": v(4.48, 2.63) * mm, "end": v(4.28, 3.27) * mm});
            skLineSegment(sketch, "E396", {"start": v(4.28, 3.27) * mm, "end": v(5.36, 3.8) * mm});
            skLineSegment(sketch, "E397", {"start": v(5.36, 3.8) * mm, "end": v(5.44, 3.86) * mm});
            skLineSegment(sketch, "E398", {"start": v(5.44, 3.86) * mm, "end": v(5.52, 3.92) * mm});
            skLineSegment(sketch, "E399", {"start": v(5.52, 3.92) * mm, "end": v(5.6, 4) * mm});
            skLineSegment(sketch, "E400", {"start": v(5.6, 4) * mm, "end": v(5.67, 4.08) * mm});
            skLineSegment(sketch, "E401", {"start": v(5.67, 4.08) * mm, "end": v(5.74, 4.15) * mm});
            skLineSegment(sketch, "E402", {"start": v(5.74, 4.15) * mm, "end": v(5.81, 4.24) * mm});
            skLineSegment(sketch, "E403", {"start": v(5.81, 4.24) * mm, "end": v(5.89, 4.34) * mm});
            skLineSegment(sketch, "E404", {"start": v(5.89, 4.34) * mm, "end": v(5.95, 4.44) * mm});
            skLineSegment(sketch, "E405", {"start": v(5.95, 4.44) * mm, "end": v(6.01, 4.53) * mm});
            skLineSegment(sketch, "E406", {"start": v(6.01, 4.53) * mm, "end": v(6.07, 4.64) * mm});
            skLineSegment(sketch, "E407", {"start": v(6.07, 4.64) * mm, "end": v(6.13, 4.76) * mm});
            skLineSegment(sketch, "E408", {"start": v(6.13, 4.76) * mm, "end": v(6.18, 4.85) * mm});
            skLineSegment(sketch, "E409", {"start": v(6.18, 4.85) * mm, "end": v(6.22, 4.95) * mm});
            skLineSegment(sketch, "E410", {"start": v(6.22, 4.95) * mm, "end": v(6.27, 5.05) * mm});
            skLineSegment(sketch, "E411", {"start": v(6.27, 5.05) * mm, "end": v(6.3, 5.16) * mm});
            skLineSegment(sketch, "E412", {"start": v(6.3, 5.16) * mm, "end": v(6.38, 5.35) * mm});
            skLineSegment(sketch, "E413", {"start": v(6.38, 5.35) * mm, "end": v(5.94, 5.95) * mm});
            skLineSegment(sketch, "E414", {"start": v(5.94, 5.95) * mm, "end": v(5.74, 5.94) * mm});
            skLineSegment(sketch, "E415", {"start": v(5.74, 5.94) * mm, "end": v(5.62, 5.94) * mm});
            skLineSegment(sketch, "E416", {"start": v(5.62, 5.94) * mm, "end": v(5.51, 5.93) * mm});
            skLineSegment(sketch, "E417", {"start": v(5.51, 5.93) * mm, "end": v(5.4, 5.92) * mm});
            skLineSegment(sketch, "E418", {"start": v(5.4, 5.92) * mm, "end": v(5.3, 5.9) * mm});
            skLineSegment(sketch, "E419", {"start": v(5.3, 5.9) * mm, "end": v(5.17, 5.88) * mm});
            skLineSegment(sketch, "E420", {"start": v(5.17, 5.88) * mm, "end": v(5.05, 5.85) * mm});
            skLineSegment(sketch, "E421", {"start": v(5.05, 5.85) * mm, "end": v(4.94, 5.83) * mm});
            skLineSegment(sketch, "E422", {"start": v(4.94, 5.83) * mm, "end": v(4.83, 5.8) * mm});
            skLineSegment(sketch, "E423", {"start": v(4.83, 5.8) * mm, "end": v(4.71, 5.76) * mm});
            skLineSegment(sketch, "E424", {"start": v(4.71, 5.76) * mm, "end": v(4.6, 5.72) * mm});
            skLineSegment(sketch, "E425", {"start": v(4.6, 5.72) * mm, "end": v(4.51, 5.68) * mm});
            skLineSegment(sketch, "E426", {"start": v(4.51, 5.68) * mm, "end": v(4.41, 5.63) * mm});
            skLineSegment(sketch, "E427", {"start": v(4.41, 5.63) * mm, "end": v(4.32, 5.58) * mm});
            skLineSegment(sketch, "E428", {"start": v(4.32, 5.58) * mm, "end": v(4.23, 5.52) * mm});
            skLineSegment(sketch, "E429", {"start": v(4.23, 5.52) * mm, "end": v(4.16, 5.46) * mm});
            skLineSegment(sketch, "E430", {"start": v(4.16, 5.46) * mm, "end": v(3.32, 4.6) * mm});
            skArc(sketch, "E431", {"start": v(3.32, 4.6) * mm, "mid": v(2.77, 4.99) * mm, "end": v(2.23, 5.39) * mm});
            skLineSegment(sketch, "E432", {"start": v(2.23, 5.39) * mm, "end": v(2.79, 6.45) * mm});
            skLineSegment(sketch, "E433", {"start": v(2.79, 6.45) * mm, "end": v(2.82, 6.54) * mm});
            skLineSegment(sketch, "E434", {"start": v(2.82, 6.54) * mm, "end": v(2.85, 6.64) * mm});
            skLineSegment(sketch, "E435", {"start": v(2.85, 6.64) * mm, "end": v(2.87, 6.75) * mm});
            skLineSegment(sketch, "E436", {"start": v(2.87, 6.75) * mm, "end": v(2.89, 6.86) * mm});
            skLineSegment(sketch, "E437", {"start": v(2.89, 6.86) * mm, "end": v(2.9, 6.96) * mm});
            skLineSegment(sketch, "E438", {"start": v(2.9, 6.96) * mm, "end": v(2.9, 7.07) * mm});
            skLineSegment(sketch, "E439", {"start": v(2.9, 7.07) * mm, "end": v(2.9, 7.2) * mm});
            skLineSegment(sketch, "E440", {"start": v(2.9, 7.2) * mm, "end": v(2.9, 7.3) * mm});
            skLineSegment(sketch, "E441", {"start": v(2.9, 7.3) * mm, "end": v(2.89, 7.43) * mm});
            skLineSegment(sketch, "E442", {"start": v(2.89, 7.43) * mm, "end": v(2.87, 7.55) * mm});
            skLineSegment(sketch, "E443", {"start": v(2.87, 7.55) * mm, "end": v(2.86, 7.68) * mm});
            skLineSegment(sketch, "E444", {"start": v(2.86, 7.68) * mm, "end": v(2.84, 7.78) * mm});
            skLineSegment(sketch, "E445", {"start": v(2.84, 7.78) * mm, "end": v(2.82, 7.88) * mm});
            skLineSegment(sketch, "E446", {"start": v(2.82, 7.88) * mm, "end": v(2.8, 8) * mm});
            skLineSegment(sketch, "E447", {"start": v(2.8, 8) * mm, "end": v(2.76, 8.1) * mm});
            skLineSegment(sketch, "E448", {"start": v(2.76, 8.1) * mm, "end": v(2.7, 8.3) * mm});
            skLineSegment(sketch, "E449", {"start": v(2.7, 8.3) * mm, "end": v(2, 8.53) * mm});
            skLineSegment(sketch, "E450", {"start": v(2, 8.53) * mm, "end": v(1.84, 8.4) * mm});
            skLineSegment(sketch, "E451", {"start": v(1.84, 8.4) * mm, "end": v(1.75, 8.33) * mm});
            skLineSegment(sketch, "E452", {"start": v(1.75, 8.33) * mm, "end": v(1.66, 8.26) * mm});
            skLineSegment(sketch, "E453", {"start": v(1.66, 8.26) * mm, "end": v(1.59, 8.19) * mm});
            skLineSegment(sketch, "E454", {"start": v(1.59, 8.19) * mm, "end": v(1.51, 8.11) * mm});
            skLineSegment(sketch, "E455", {"start": v(1.51, 8.11) * mm, "end": v(1.42, 8.02) * mm});
            skLineSegment(sketch, "E456", {"start": v(1.42, 8.02) * mm, "end": v(1.34, 7.93) * mm});
            skLineSegment(sketch, "E457", {"start": v(1.34, 7.93) * mm, "end": v(1.26, 7.84) * mm});
            skLineSegment(sketch, "E458", {"start": v(1.26, 7.84) * mm, "end": v(1.2, 7.75) * mm});
            skLineSegment(sketch, "E459", {"start": v(1.2, 7.75) * mm, "end": v(1.12, 7.65) * mm});
            skLineSegment(sketch, "E460", {"start": v(1.12, 7.65) * mm, "end": v(1.06, 7.56) * mm});
            skLineSegment(sketch, "E461", {"start": v(1.06, 7.56) * mm, "end": v(1, 7.47) * mm});
            skLineSegment(sketch, "E462", {"start": v(1, 7.47) * mm, "end": v(0.95, 7.37) * mm});
            skLineSegment(sketch, "E463", {"start": v(0.95, 7.37) * mm, "end": v(0.9, 7.28) * mm});
            skLineSegment(sketch, "E464", {"start": v(0.9, 7.28) * mm, "end": v(0.87, 7.18) * mm});
            skLineSegment(sketch, "E465", {"start": v(0.87, 7.18) * mm, "end": v(0.85, 7.08) * mm});
            skLineSegment(sketch, "E466", {"start": v(0.85, 7.08) * mm, "end": v(0.67, 5.89) * mm});
            skArc(sketch, "E467", {"start": v(0.67, 5.89) * mm, "mid": v(0, 5.89) * mm, "end": v(-0.67, 5.89) * mm});
            skLineSegment(sketch, "E468", {"start": v(-0.67, 5.89) * mm, "end": v(-0.85, 7.08) * mm});
            skLineSegment(sketch, "E469", {"start": v(-0.85, 7.08) * mm, "end": v(-0.87, 7.18) * mm});
            skLineSegment(sketch, "E470", {"start": v(-0.87, 7.18) * mm, "end": v(-0.9, 7.28) * mm});
            skLineSegment(sketch, "E471", {"start": v(-0.9, 7.28) * mm, "end": v(-0.95, 7.37) * mm});
            skLineSegment(sketch, "E472", {"start": v(-0.95, 7.37) * mm, "end": v(-1, 7.47) * mm});
            skLineSegment(sketch, "E473", {"start": v(-1, 7.47) * mm, "end": v(-1.06, 7.56) * mm});
            skLineSegment(sketch, "E474", {"start": v(-1.06, 7.56) * mm, "end": v(-1.12, 7.65) * mm});
            skLineSegment(sketch, "E475", {"start": v(-1.12, 7.65) * mm, "end": v(-1.2, 7.75) * mm});
            skLineSegment(sketch, "E476", {"start": v(-1.2, 7.75) * mm, "end": v(-1.26, 7.84) * mm});
            skLineSegment(sketch, "E477", {"start": v(-1.26, 7.84) * mm, "end": v(-1.34, 7.93) * mm});
            skLineSegment(sketch, "E478", {"start": v(-1.34, 7.93) * mm, "end": v(-1.42, 8.02) * mm});
            skLineSegment(sketch, "E479", {"start": v(-1.42, 8.02) * mm, "end": v(-1.51, 8.11) * mm});
            skLineSegment(sketch, "E480", {"start": v(-1.51, 8.11) * mm, "end": v(-1.59, 8.19) * mm});
            skLineSegment(sketch, "E481", {"start": v(-1.59, 8.19) * mm, "end": v(-1.66, 8.26) * mm});
            skLineSegment(sketch, "E482", {"start": v(-1.66, 8.26) * mm, "end": v(-1.75, 8.33) * mm});
            skLineSegment(sketch, "E483", {"start": v(-1.75, 8.33) * mm, "end": v(-1.84, 8.4) * mm});
            skLineSegment(sketch, "E484", {"start": v(-1.84, 8.4) * mm, "end": v(-2, 8.53) * mm});
            skLineSegment(sketch, "E485", {"start": v(-2, 8.53) * mm, "end": v(-2.7, 8.3) * mm});
            skLineSegment(sketch, "E486", {"start": v(-2.7, 8.3) * mm, "end": v(-2.76, 8.1) * mm});
            skLineSegment(sketch, "E487", {"start": v(-2.76, 8.1) * mm, "end": v(-2.8, 8) * mm});
            skLineSegment(sketch, "E488", {"start": v(-2.8, 8) * mm, "end": v(-2.82, 7.88) * mm});
            skLineSegment(sketch, "E489", {"start": v(-2.82, 7.88) * mm, "end": v(-2.84, 7.78) * mm});
            skLineSegment(sketch, "E490", {"start": v(-2.84, 7.78) * mm, "end": v(-2.86, 7.68) * mm});
            skLineSegment(sketch, "E491", {"start": v(-2.86, 7.68) * mm, "end": v(-2.87, 7.55) * mm});
            skLineSegment(sketch, "E492", {"start": v(-2.87, 7.55) * mm, "end": v(-2.89, 7.43) * mm});
            skLineSegment(sketch, "E493", {"start": v(-2.89, 7.43) * mm, "end": v(-2.9, 7.3) * mm});
            skLineSegment(sketch, "E494", {"start": v(-2.9, 7.3) * mm, "end": v(-2.9, 7.2) * mm});
            skLineSegment(sketch, "E495", {"start": v(-2.9, 7.2) * mm, "end": v(-2.9, 7.07) * mm});
            skLineSegment(sketch, "E496", {"start": v(-2.9, 7.07) * mm, "end": v(-2.9, 6.96) * mm});
            skLineSegment(sketch, "E497", {"start": v(-2.9, 6.96) * mm, "end": v(-2.89, 6.86) * mm});
            skLineSegment(sketch, "E498", {"start": v(-2.89, 6.86) * mm, "end": v(-2.87, 6.75) * mm});
            skLineSegment(sketch, "E499", {"start": v(-2.87, 6.75) * mm, "end": v(-2.85, 6.64) * mm});
            skLineSegment(sketch, "E500", {"start": v(-2.85, 6.64) * mm, "end": v(-2.82, 6.54) * mm});
            skLineSegment(sketch, "E501", {"start": v(-2.82, 6.54) * mm, "end": v(-2.79, 6.45) * mm});
            skLineSegment(sketch, "E502", {"start": v(-2.79, 6.45) * mm, "end": v(-2.23, 5.39) * mm});
            skArc(sketch, "E503", {"start": v(-2.23, 5.39) * mm, "mid": v(-2.77, 4.99) * mm, "end": v(-3.32, 4.6) * mm});
            skLineSegment(sketch, "E504", {"start": v(-3.32, 4.6) * mm, "end": v(-4.16, 5.46) * mm});
            skLineSegment(sketch, "E505", {"start": v(-4.16, 5.46) * mm, "end": v(-4.23, 5.52) * mm});
            skLineSegment(sketch, "E506", {"start": v(-4.23, 5.52) * mm, "end": v(-4.32, 5.58) * mm});
            skLineSegment(sketch, "E507", {"start": v(-4.32, 5.58) * mm, "end": v(-4.41, 5.63) * mm});
            skLineSegment(sketch, "E508", {"start": v(-4.41, 5.63) * mm, "end": v(-4.51, 5.68) * mm});
            skLineSegment(sketch, "E509", {"start": v(-4.51, 5.68) * mm, "end": v(-4.6, 5.72) * mm});
            skLineSegment(sketch, "E510", {"start": v(-4.6, 5.72) * mm, "end": v(-4.71, 5.76) * mm});
            skLineSegment(sketch, "E511", {"start": v(-4.71, 5.76) * mm, "end": v(-4.83, 5.8) * mm});
            skLineSegment(sketch, "E512", {"start": v(-4.83, 5.8) * mm, "end": v(-4.94, 5.83) * mm});
            skLineSegment(sketch, "E513", {"start": v(-4.94, 5.83) * mm, "end": v(-5.05, 5.85) * mm});
            skLineSegment(sketch, "E514", {"start": v(-5.05, 5.85) * mm, "end": v(-5.17, 5.88) * mm});
            skLineSegment(sketch, "E515", {"start": v(-5.17, 5.88) * mm, "end": v(-5.3, 5.9) * mm});
            skLineSegment(sketch, "E516", {"start": v(-5.3, 5.9) * mm, "end": v(-5.4, 5.92) * mm});
            skLineSegment(sketch, "E517", {"start": v(-5.4, 5.92) * mm, "end": v(-5.51, 5.93) * mm});
            skLineSegment(sketch, "E518", {"start": v(-5.51, 5.93) * mm, "end": v(-5.62, 5.94) * mm});
            skLineSegment(sketch, "E519", {"start": v(-5.62, 5.94) * mm, "end": v(-5.74, 5.94) * mm});
            skLineSegment(sketch, "E520", {"start": v(-5.74, 5.94) * mm, "end": v(-5.94, 5.95) * mm});
            skLineSegment(sketch, "E521", {"start": v(-5.94, 5.95) * mm, "end": v(-6.38, 5.35) * mm});
            skLineSegment(sketch, "E522", {"start": v(-6.38, 5.35) * mm, "end": v(-6.3, 5.16) * mm});
            skLineSegment(sketch, "E523", {"start": v(-6.3, 5.16) * mm, "end": v(-6.27, 5.05) * mm});
            skLineSegment(sketch, "E524", {"start": v(-6.27, 5.05) * mm, "end": v(-6.22, 4.95) * mm});
            skLineSegment(sketch, "E525", {"start": v(-6.22, 4.95) * mm, "end": v(-6.18, 4.85) * mm});
            skLineSegment(sketch, "E526", {"start": v(-6.18, 4.85) * mm, "end": v(-6.13, 4.76) * mm});
            skLineSegment(sketch, "E527", {"start": v(-6.13, 4.76) * mm, "end": v(-6.07, 4.64) * mm});
            skLineSegment(sketch, "E528", {"start": v(-6.07, 4.64) * mm, "end": v(-6.01, 4.53) * mm});
            skLineSegment(sketch, "E529", {"start": v(-6.01, 4.53) * mm, "end": v(-5.95, 4.44) * mm});
            skLineSegment(sketch, "E530", {"start": v(-5.95, 4.44) * mm, "end": v(-5.89, 4.34) * mm});
            skLineSegment(sketch, "E531", {"start": v(-5.89, 4.34) * mm, "end": v(-5.81, 4.24) * mm});
            skLineSegment(sketch, "E532", {"start": v(-5.81, 4.24) * mm, "end": v(-5.74, 4.15) * mm});
            skLineSegment(sketch, "E533", {"start": v(-5.74, 4.15) * mm, "end": v(-5.67, 4.08) * mm});
            skLineSegment(sketch, "E534", {"start": v(-5.67, 4.08) * mm, "end": v(-5.6, 4) * mm});
            skLineSegment(sketch, "E535", {"start": v(-5.6, 4) * mm, "end": v(-5.52, 3.92) * mm});
            skLineSegment(sketch, "E536", {"start": v(-5.52, 3.92) * mm, "end": v(-5.44, 3.86) * mm});
            skLineSegment(sketch, "E537", {"start": v(-5.44, 3.86) * mm, "end": v(-5.36, 3.8) * mm});
            skLineSegment(sketch, "E538", {"start": v(-5.36, 3.8) * mm, "end": v(-4.28, 3.27) * mm});
            skArc(sketch, "E539", {"start": v(-4.28, 3.27) * mm, "mid": v(-4.48, 2.63) * mm, "end": v(-4.7, 1.99) * mm});
            skLineSegment(sketch, "E540", {"start": v(-4.7, 1.99) * mm, "end": v(-5.88, 2.2) * mm});
            skLineSegment(sketch, "E541", {"start": v(-5.88, 2.2) * mm, "end": v(-5.98, 2.2) * mm});
            skLineSegment(sketch, "E542", {"start": v(-5.98, 2.2) * mm, "end": v(-6.08, 2.2) * mm});
            skLineSegment(sketch, "E543", {"start": v(-6.08, 2.2) * mm, "end": v(-6.19, 2.18) * mm});
            skLineSegment(sketch, "E544", {"start": v(-6.19, 2.18) * mm, "end": v(-6.3, 2.16) * mm});
            skLineSegment(sketch, "E545", {"start": v(-6.3, 2.16) * mm, "end": v(-6.4, 2.14) * mm});
            skLineSegment(sketch, "E546", {"start": v(-6.4, 2.14) * mm, "end": v(-6.5, 2.1) * mm});
            skLineSegment(sketch, "E547", {"start": v(-6.5, 2.1) * mm, "end": v(-6.63, 2.07) * mm});
            skLineSegment(sketch, "E548", {"start": v(-6.63, 2.07) * mm, "end": v(-6.73, 2.03) * mm});
            skLineSegment(sketch, "E549", {"start": v(-6.73, 2.03) * mm, "end": v(-6.84, 1.99) * mm});
            skLineSegment(sketch, "E550", {"start": v(-6.84, 1.99) * mm, "end": v(-6.95, 1.94) * mm});
            skLineSegment(sketch, "E551", {"start": v(-6.95, 1.94) * mm, "end": v(-7.07, 1.88) * mm});
            skLineSegment(sketch, "E552", {"start": v(-7.07, 1.88) * mm, "end": v(-7.16, 1.83) * mm});
            skLineSegment(sketch, "E553", {"start": v(-7.16, 1.83) * mm, "end": v(-7.25, 1.78) * mm});
            skLineSegment(sketch, "E554", {"start": v(-7.25, 1.78) * mm, "end": v(-7.35, 1.72) * mm});
            skLineSegment(sketch, "E555", {"start": v(-7.35, 1.72) * mm, "end": v(-7.44, 1.66) * mm});
            skLineSegment(sketch, "E556", {"start": v(-7.44, 1.66) * mm, "end": v(-7.61, 1.55) * mm});
            skLineSegment(sketch, "E557", {"start": v(-7.61, 1.55) * mm, "end": v(-7.61, 0.8) * mm});
            skLineSegment(sketch, "E558", {"start": v(-7.61, 0.8) * mm, "end": v(-7.44, 0.69) * mm});
            skLineSegment(sketch, "E559", {"start": v(-7.44, 0.69) * mm, "end": v(-7.35, 0.63) * mm});
            skLineSegment(sketch, "E560", {"start": v(-7.35, 0.63) * mm, "end": v(-7.25, 0.57) * mm});
            skLineSegment(sketch, "E561", {"start": v(-7.25, 0.57) * mm, "end": v(-7.16, 0.52) * mm});
            skLineSegment(sketch, "E562", {"start": v(-7.16, 0.52) * mm, "end": v(-7.07, 0.47) * mm});
            skLineSegment(sketch, "E563", {"start": v(-7.07, 0.47) * mm, "end": v(-6.95, 0.4) * mm});
            skLineSegment(sketch, "E564", {"start": v(-6.95, 0.4) * mm, "end": v(-6.84, 0.36) * mm});
            skLineSegment(sketch, "E565", {"start": v(-6.84, 0.36) * mm, "end": v(-6.73, 0.32) * mm});
            skLineSegment(sketch, "E566", {"start": v(-6.73, 0.32) * mm, "end": v(-6.63, 0.28) * mm});
            skLineSegment(sketch, "E567", {"start": v(-6.63, 0.28) * mm, "end": v(-6.5, 0.24) * mm});
            skLineSegment(sketch, "E568", {"start": v(-6.5, 0.24) * mm, "end": v(-6.4, 0.2) * mm});
            skLineSegment(sketch, "E569", {"start": v(-6.4, 0.2) * mm, "end": v(-6.3, 0.19) * mm});
            skLineSegment(sketch, "E570", {"start": v(-6.3, 0.19) * mm, "end": v(-6.19, 0.17) * mm});
            skLineSegment(sketch, "E571", {"start": v(-6.19, 0.17) * mm, "end": v(-6.08, 0.15) * mm});
            skLineSegment(sketch, "E572", {"start": v(-6.08, 0.15) * mm, "end": v(-5.98, 0.15) * mm});
            skLineSegment(sketch, "E573", {"start": v(-5.98, 0.15) * mm, "end": v(-5.88, 0.15) * mm});
            skLineSegment(sketch, "E574", {"start": v(-5.88, 0.15) * mm, "end": v(-4.7, 0.36) * mm});
            skArc(sketch, "E575", {"start": v(-4.7, 0.36) * mm, "mid": v(-4.48, -0.28) * mm, "end": v(-4.28, -0.92) * mm});
            skLineSegment(sketch, "E576", {"start": v(-4.28, -0.92) * mm, "end": v(-5.36, -1.45) * mm});
            skLineSegment(sketch, "E577", {"start": v(-5.36, -1.45) * mm, "end": v(-5.44, -1.5) * mm});
            skLineSegment(sketch, "E578", {"start": v(-5.44, -1.5) * mm, "end": v(-5.52, -1.57) * mm});
            skLineSegment(sketch, "E579", {"start": v(-5.52, -1.57) * mm, "end": v(-5.6, -1.65) * mm});
            skLineSegment(sketch, "E580", {"start": v(-5.6, -1.65) * mm, "end": v(-5.67, -1.73) * mm});
            skLineSegment(sketch, "E581", {"start": v(-5.67, -1.73) * mm, "end": v(-5.74, -1.8) * mm});
            skLineSegment(sketch, "E582", {"start": v(-5.74, -1.8) * mm, "end": v(-5.81, -1.9) * mm});
            skLineSegment(sketch, "E583", {"start": v(-5.81, -1.9) * mm, "end": v(-5.89, -2) * mm});
            skLineSegment(sketch, "E584", {"start": v(-5.89, -2) * mm, "end": v(-5.95, -2.09) * mm});
            skLineSegment(sketch, "E585", {"start": v(-5.95, -2.09) * mm, "end": v(-6.01, -2.18) * mm});
            skLineSegment(sketch, "E586", {"start": v(-6.01, -2.18) * mm, "end": v(-6.07, -2.3) * mm});
            skLineSegment(sketch, "E587", {"start": v(-6.07, -2.3) * mm, "end": v(-6.13, -2.4) * mm});
            skLineSegment(sketch, "E588", {"start": v(-6.13, -2.4) * mm, "end": v(-6.18, -2.5) * mm});
            skLineSegment(sketch, "E589", {"start": v(-6.18, -2.5) * mm, "end": v(-6.22, -2.6) * mm});
            skLineSegment(sketch, "E590", {"start": v(-6.22, -2.6) * mm, "end": v(-6.27, -2.7) * mm});
            skLineSegment(sketch, "E591", {"start": v(-6.27, -2.7) * mm, "end": v(-6.3, -2.8) * mm});
            skLineSegment(sketch, "E592", {"start": v(-6.3, -2.8) * mm, "end": v(-6.38, -3) * mm});
            skLineSegment(sketch, "E593", {"start": v(-6.38, -3) * mm, "end": v(-5.94, -3.6) * mm});
            skLineSegment(sketch, "E594", {"start": v(-5.94, -3.6) * mm, "end": v(-5.74, -3.6) * mm});
            skLineSegment(sketch, "E595", {"start": v(-5.74, -3.6) * mm, "end": v(-5.62, -3.59) * mm});
            skLineSegment(sketch, "E596", {"start": v(-5.62, -3.59) * mm, "end": v(-5.51, -3.58) * mm});
            skLineSegment(sketch, "E597", {"start": v(-5.51, -3.58) * mm, "end": v(-5.4, -3.57) * mm});
            skLineSegment(sketch, "E598", {"start": v(-5.4, -3.57) * mm, "end": v(-5.3, -3.55) * mm});
            skLineSegment(sketch, "E599", {"start": v(-5.3, -3.55) * mm, "end": v(-5.17, -3.53) * mm});
            skLineSegment(sketch, "E600", {"start": v(-5.17, -3.53) * mm, "end": v(-5.05, -3.5) * mm});
            skLineSegment(sketch, "E601", {"start": v(-5.05, -3.5) * mm, "end": v(-4.94, -3.48) * mm});
            skLineSegment(sketch, "E602", {"start": v(-4.94, -3.48) * mm, "end": v(-4.83, -3.45) * mm});
            skLineSegment(sketch, "E603", {"start": v(-4.83, -3.45) * mm, "end": v(-4.71, -3.4) * mm});
            skLineSegment(sketch, "E604", {"start": v(-4.71, -3.4) * mm, "end": v(-4.6, -3.37) * mm});
            skLineSegment(sketch, "E605", {"start": v(-4.6, -3.37) * mm, "end": v(-4.51, -3.33) * mm});
            skLineSegment(sketch, "E606", {"start": v(-4.51, -3.33) * mm, "end": v(-4.41, -3.28) * mm});
            skLineSegment(sketch, "E607", {"start": v(-4.41, -3.28) * mm, "end": v(-4.32, -3.23) * mm});
            skLineSegment(sketch, "E608", {"start": v(-4.32, -3.23) * mm, "end": v(-4.23, -3.17) * mm});
            skLineSegment(sketch, "E609", {"start": v(-4.23, -3.17) * mm, "end": v(-4.16, -3.1) * mm});
            skLineSegment(sketch, "E610", {"start": v(-4.16, -3.1) * mm, "end": v(-3.32, -2.24) * mm});
            skArc(sketch, "E611", {"start": v(-3.32, -2.24) * mm, "mid": v(-2.77, -2.64) * mm, "end": v(-2.23, -3.04) * mm});
            skLineSegment(sketch, "E612", {"start": v(-2.23, -3.04) * mm, "end": v(-2.79, -4.1) * mm});
            skLineSegment(sketch, "E613", {"start": v(-2.79, -4.1) * mm, "end": v(-2.82, -4.2) * mm});
            skLineSegment(sketch, "E614", {"start": v(-2.82, -4.2) * mm, "end": v(-2.85, -4.3) * mm});
            skLineSegment(sketch, "E615", {"start": v(-2.85, -4.3) * mm, "end": v(-2.87, -4.4) * mm});
            skLineSegment(sketch, "E616", {"start": v(-2.87, -4.4) * mm, "end": v(-2.89, -4.5) * mm});
            skLineSegment(sketch, "E617", {"start": v(-2.89, -4.5) * mm, "end": v(-2.9, -4.61) * mm});
            skLineSegment(sketch, "E618", {"start": v(-2.9, -4.61) * mm, "end": v(-2.9, -4.73) * mm});
            skLineSegment(sketch, "E619", {"start": v(-2.9, -4.73) * mm, "end": v(-2.9, -4.85) * mm});
            skLineSegment(sketch, "E620", {"start": v(-2.9, -4.85) * mm, "end": v(-2.9, -4.96) * mm});
            skLineSegment(sketch, "E621", {"start": v(-2.9, -4.96) * mm, "end": v(-2.89, -5.08) * mm});
            skLineSegment(sketch, "E622", {"start": v(-2.89, -5.08) * mm, "end": v(-2.87, -5.2) * mm});
            skLineSegment(sketch, "E623", {"start": v(-2.87, -5.2) * mm, "end": v(-2.86, -5.33) * mm});
            skLineSegment(sketch, "E624", {"start": v(-2.86, -5.33) * mm, "end": v(-2.84, -5.43) * mm});
            skLineSegment(sketch, "E625", {"start": v(-2.84, -5.43) * mm, "end": v(-2.82, -5.54) * mm});
            skLineSegment(sketch, "E626", {"start": v(-2.82, -5.54) * mm, "end": v(-2.8, -5.64) * mm});
            skLineSegment(sketch, "E627", {"start": v(-2.8, -5.64) * mm, "end": v(-2.76, -5.76) * mm});
            skLineSegment(sketch, "E628", {"start": v(-2.76, -5.76) * mm, "end": v(-2.7, -5.95) * mm});
            skLineSegment(sketch, "E629", {"start": v(-2.7, -5.95) * mm, "end": v(-2, -6.18) * mm});
            skLineSegment(sketch, "E630", {"start": v(-2, -6.18) * mm, "end": v(-1.84, -6.06) * mm});
            skLineSegment(sketch, "E631", {"start": v(-1.84, -6.06) * mm, "end": v(-1.75, -5.98) * mm});
            skLineSegment(sketch, "E632", {"start": v(-1.75, -5.98) * mm, "end": v(-1.66, -5.9) * mm});
            skLineSegment(sketch, "E633", {"start": v(-1.66, -5.9) * mm, "end": v(-1.59, -5.84) * mm});
            skLineSegment(sketch, "E634", {"start": v(-1.59, -5.84) * mm, "end": v(-1.51, -5.77) * mm});
            skLineSegment(sketch, "E635", {"start": v(-1.51, -5.77) * mm, "end": v(-1.42, -5.67) * mm});
            skLineSegment(sketch, "E636", {"start": v(-1.42, -5.67) * mm, "end": v(-1.34, -5.58) * mm});
            skLineSegment(sketch, "E637", {"start": v(-1.34, -5.58) * mm, "end": v(-1.26, -5.5) * mm});
            skLineSegment(sketch, "E638", {"start": v(-1.26, -5.5) * mm, "end": v(-1.2, -5.4) * mm});
            skLineSegment(sketch, "E639", {"start": v(-1.2, -5.4) * mm, "end": v(-1.12, -5.3) * mm});
            skLineSegment(sketch, "E640", {"start": v(-1.12, -5.3) * mm, "end": v(-1.06, -5.2) * mm});
            skLineSegment(sketch, "E641", {"start": v(-1.06, -5.2) * mm, "end": v(-1, -5.12) * mm});
            skLineSegment(sketch, "E642", {"start": v(-1, -5.12) * mm, "end": v(-0.95, -5.02) * mm});
            skLineSegment(sketch, "E643", {"start": v(-0.95, -5.02) * mm, "end": v(-0.9, -4.93) * mm});
            skLineSegment(sketch, "E644", {"start": v(-0.9, -4.93) * mm, "end": v(-0.87, -4.83) * mm});
            skLineSegment(sketch, "E645", {"start": v(-0.87, -4.83) * mm, "end": v(-0.85, -4.73) * mm});
            skLineSegment(sketch, "E646", {"start": v(-0.85, -4.73) * mm, "end": v(-0.67, -3.54) * mm});
            skArc(sketch, "E647", {"start": v(-0.67, -3.54) * mm, "mid": v(0, -3.54) * mm, "end": v(0.67, -3.54) * mm});
            skLineSegment(sketch, "E648", {"start": v(0.67, -3.54) * mm, "end": v(0.85, -4.73) * mm});
            skLineSegment(sketch, "E649", {"start": v(0.85, -4.73) * mm, "end": v(0.87, -4.83) * mm});
            skLineSegment(sketch, "E650", {"start": v(0.87, -4.83) * mm, "end": v(0.9, -4.93) * mm});
            skLineSegment(sketch, "E651", {"start": v(0.9, -4.93) * mm, "end": v(0.95, -5.02) * mm});
            skLineSegment(sketch, "E652", {"start": v(0.95, -5.02) * mm, "end": v(1, -5.12) * mm});
            skLineSegment(sketch, "E653", {"start": v(1, -5.12) * mm, "end": v(1.06, -5.2) * mm});
            skLineSegment(sketch, "E654", {"start": v(1.06, -5.2) * mm, "end": v(1.12, -5.3) * mm});
            skLineSegment(sketch, "E655", {"start": v(1.12, -5.3) * mm, "end": v(1.2, -5.4) * mm});
            skLineSegment(sketch, "E656", {"start": v(1.2, -5.4) * mm, "end": v(1.26, -5.5) * mm});
            skLineSegment(sketch, "E657", {"start": v(1.26, -5.5) * mm, "end": v(1.34, -5.58) * mm});
            skLineSegment(sketch, "E658", {"start": v(1.34, -5.58) * mm, "end": v(1.42, -5.67) * mm});
            skLineSegment(sketch, "E659", {"start": v(1.42, -5.67) * mm, "end": v(1.51, -5.77) * mm});
            skLineSegment(sketch, "E660", {"start": v(1.51, -5.77) * mm, "end": v(1.59, -5.84) * mm});
            skLineSegment(sketch, "E661", {"start": v(1.59, -5.84) * mm, "end": v(1.66, -5.9) * mm});
            skLineSegment(sketch, "E662", {"start": v(1.66, -5.9) * mm, "end": v(1.75, -5.98) * mm});
            skLineSegment(sketch, "E663", {"start": v(1.75, -5.98) * mm, "end": v(1.84, -6.06) * mm});
            skLineSegment(sketch, "E664", {"start": v(1.84, -6.06) * mm, "end": v(2, -6.18) * mm});
            skLineSegment(sketch, "E665", {"start": v(2, -6.18) * mm, "end": v(2.7, -5.95) * mm});
            skLineSegment(sketch, "E666", {"start": v(2.7, -5.95) * mm, "end": v(2.76, -5.76) * mm});
            skLineSegment(sketch, "E667", {"start": v(2.76, -5.76) * mm, "end": v(2.8, -5.64) * mm});
            skLineSegment(sketch, "E668", {"start": v(2.8, -5.64) * mm, "end": v(2.82, -5.54) * mm});
            skLineSegment(sketch, "E669", {"start": v(2.82, -5.54) * mm, "end": v(2.84, -5.43) * mm});
            skLineSegment(sketch, "E670", {"start": v(2.84, -5.43) * mm, "end": v(2.86, -5.33) * mm});
            skLineSegment(sketch, "E671", {"start": v(2.86, -5.33) * mm, "end": v(2.87, -5.2) * mm});
            skLineSegment(sketch, "E672", {"start": v(2.87, -5.2) * mm, "end": v(2.89, -5.08) * mm});
            skLineSegment(sketch, "E673", {"start": v(2.89, -5.08) * mm, "end": v(2.9, -4.96) * mm});
            skLineSegment(sketch, "E674", {"start": v(2.9, -4.96) * mm, "end": v(2.9, -4.85) * mm});
            skLineSegment(sketch, "E675", {"start": v(2.9, -4.85) * mm, "end": v(2.9, -4.73) * mm});
            skLineSegment(sketch, "E676", {"start": v(2.9, -4.73) * mm, "end": v(2.9, -4.61) * mm});
            skLineSegment(sketch, "E677", {"start": v(2.9, -4.61) * mm, "end": v(2.89, -4.5) * mm});
            skLineSegment(sketch, "E678", {"start": v(2.89, -4.5) * mm, "end": v(2.87, -4.4) * mm});
            skLineSegment(sketch, "E679", {"start": v(2.87, -4.4) * mm, "end": v(2.85, -4.3) * mm});
            skLineSegment(sketch, "E680", {"start": v(2.85, -4.3) * mm, "end": v(2.82, -4.2) * mm});
            skLineSegment(sketch, "E681", {"start": v(2.82, -4.2) * mm, "end": v(2.79, -4.1) * mm});
            skLineSegment(sketch, "E682", {"start": v(2.79, -4.1) * mm, "end": v(2.23, -3.04) * mm});
            skArc(sketch, "E683", {"start": v(2.23, -3.04) * mm, "mid": v(2.77, -2.64) * mm, "end": v(3.32, -2.24) * mm});
            skLineSegment(sketch, "E684", {"start": v(3.32, -2.24) * mm, "end": v(4.16, -3.1) * mm});
            skLineSegment(sketch, "E685", {"start": v(4.16, -3.1) * mm, "end": v(4.23, -3.17) * mm});
            skLineSegment(sketch, "E686", {"start": v(4.23, -3.17) * mm, "end": v(4.32, -3.23) * mm});
            skLineSegment(sketch, "E687", {"start": v(4.32, -3.23) * mm, "end": v(4.41, -3.28) * mm});
            skLineSegment(sketch, "E688", {"start": v(4.41, -3.28) * mm, "end": v(4.51, -3.33) * mm});
            skLineSegment(sketch, "E689", {"start": v(4.51, -3.33) * mm, "end": v(4.6, -3.37) * mm});
            skLineSegment(sketch, "E690", {"start": v(4.6, -3.37) * mm, "end": v(4.71, -3.4) * mm});
            skLineSegment(sketch, "E691", {"start": v(4.71, -3.4) * mm, "end": v(4.83, -3.45) * mm});
            skLineSegment(sketch, "E692", {"start": v(4.83, -3.45) * mm, "end": v(4.94, -3.48) * mm});
            skLineSegment(sketch, "E693", {"start": v(4.94, -3.48) * mm, "end": v(5.05, -3.5) * mm});
            skLineSegment(sketch, "E694", {"start": v(5.05, -3.5) * mm, "end": v(5.17, -3.53) * mm});
            skLineSegment(sketch, "E695", {"start": v(5.17, -3.53) * mm, "end": v(5.3, -3.55) * mm});
            skLineSegment(sketch, "E696", {"start": v(5.3, -3.55) * mm, "end": v(5.4, -3.57) * mm});
            skLineSegment(sketch, "E697", {"start": v(5.4, -3.57) * mm, "end": v(5.51, -3.58) * mm});
            skLineSegment(sketch, "E698", {"start": v(5.51, -3.58) * mm, "end": v(5.62, -3.59) * mm});
            skLineSegment(sketch, "E699", {"start": v(5.62, -3.59) * mm, "end": v(5.74, -3.6) * mm});
            skLineSegment(sketch, "E700", {"start": v(5.74, -3.6) * mm, "end": v(5.94, -3.6) * mm});
            skLineSegment(sketch, "E701", {"start": v(5.94, -3.6) * mm, "end": v(6.38, -3) * mm});
            skLineSegment(sketch, "E702", {"start": v(6.38, -3) * mm, "end": v(6.3, -2.8) * mm});
            skLineSegment(sketch, "E703", {"start": v(6.3, -2.8) * mm, "end": v(6.27, -2.7) * mm});
            skLineSegment(sketch, "E704", {"start": v(6.27, -2.7) * mm, "end": v(6.22, -2.6) * mm});
            skLineSegment(sketch, "E705", {"start": v(6.22, -2.6) * mm, "end": v(6.18, -2.5) * mm});
            skLineSegment(sketch, "E706", {"start": v(6.18, -2.5) * mm, "end": v(6.13, -2.4) * mm});
            skLineSegment(sketch, "E707", {"start": v(6.13, -2.4) * mm, "end": v(6.07, -2.3) * mm});
            skLineSegment(sketch, "E708", {"start": v(6.07, -2.3) * mm, "end": v(6.01, -2.18) * mm});
            skLineSegment(sketch, "E709", {"start": v(6.01, -2.18) * mm, "end": v(5.95, -2.09) * mm});
            skLineSegment(sketch, "E710", {"start": v(5.95, -2.09) * mm, "end": v(5.89, -2) * mm});
            skLineSegment(sketch, "E711", {"start": v(5.89, -2) * mm, "end": v(5.81, -1.9) * mm});
            skLineSegment(sketch, "E712", {"start": v(5.81, -1.9) * mm, "end": v(5.74, -1.8) * mm});
            skLineSegment(sketch, "E713", {"start": v(5.74, -1.8) * mm, "end": v(5.67, -1.73) * mm});
            skLineSegment(sketch, "E714", {"start": v(5.67, -1.73) * mm, "end": v(5.6, -1.65) * mm});
            skLineSegment(sketch, "E715", {"start": v(5.6, -1.65) * mm, "end": v(5.52, -1.57) * mm});
            skLineSegment(sketch, "E716", {"start": v(5.52, -1.57) * mm, "end": v(5.44, -1.5) * mm});
            skLineSegment(sketch, "E717", {"start": v(5.44, -1.5) * mm, "end": v(5.36, -1.45) * mm});
            skLineSegment(sketch, "E718", {"start": v(5.36, -1.45) * mm, "end": v(4.28, -0.92) * mm});
            skArc(sketch, "E719", {"start": v(4.28, -0.92) * mm, "mid": v(4.48, -0.28) * mm, "end": v(4.7, 0.36) * mm});
            skSolve(sketch);
        }
        {
            var Q0;
            Q0 = qSketchRegion(id + "F0", true);
            var Q1;
            Q1 = qSketchRegion(id + "F2", true);
            loft(context, id + "F3", {"sheetProfilesArray" : [{ "sheetProfileEntities" : qUnion([Q0]) }, { "sheetProfileEntities" : qUnion([Q1]) }]});
        }
        {
            var Q0;
            Q0=makeQuery(id+"F3.opLoft","CAP_FACE",FACE,{"disambiguationData":[OSD([makeQuery(id+"F2.imprint","IMPRINT",FACE,{"disambiguationData":[TD([[makeQuery(id+"F2.imprint","IMPRINT",EDGE,{"derivedFrom":sQuery(id+"F2.wireOp",EDGE,"E360")}),1.0]])]})])],"isStart":true});
            var sketch = newSketch(context, id + "F4", { "sketchPlane" : qUnion([Q0])});
            skCircle(sketch, "E720", {"center": v(0, 1.82) * mm, "radius": 2.95 * mm});
            skSolve(sketch);
        }
        {
            var Q0;
            Q0=makeQuery(id+"F4.imprint","IMPRINT",FACE,{"disambiguationData":[TD([[makeQuery(id+"F4.imprint","IMPRINT",EDGE,{"derivedFrom":sQuery(id+"F4.wireOp",EDGE,"E720")}),1.0]])]});
            extrude(context, id + "F5", {"entities" : qUnion([Q0]), "operationType" : NewBodyOperationType.REMOVE, "oppositeDirection" : true, "depth" : 250 * mm});
        }
    });
